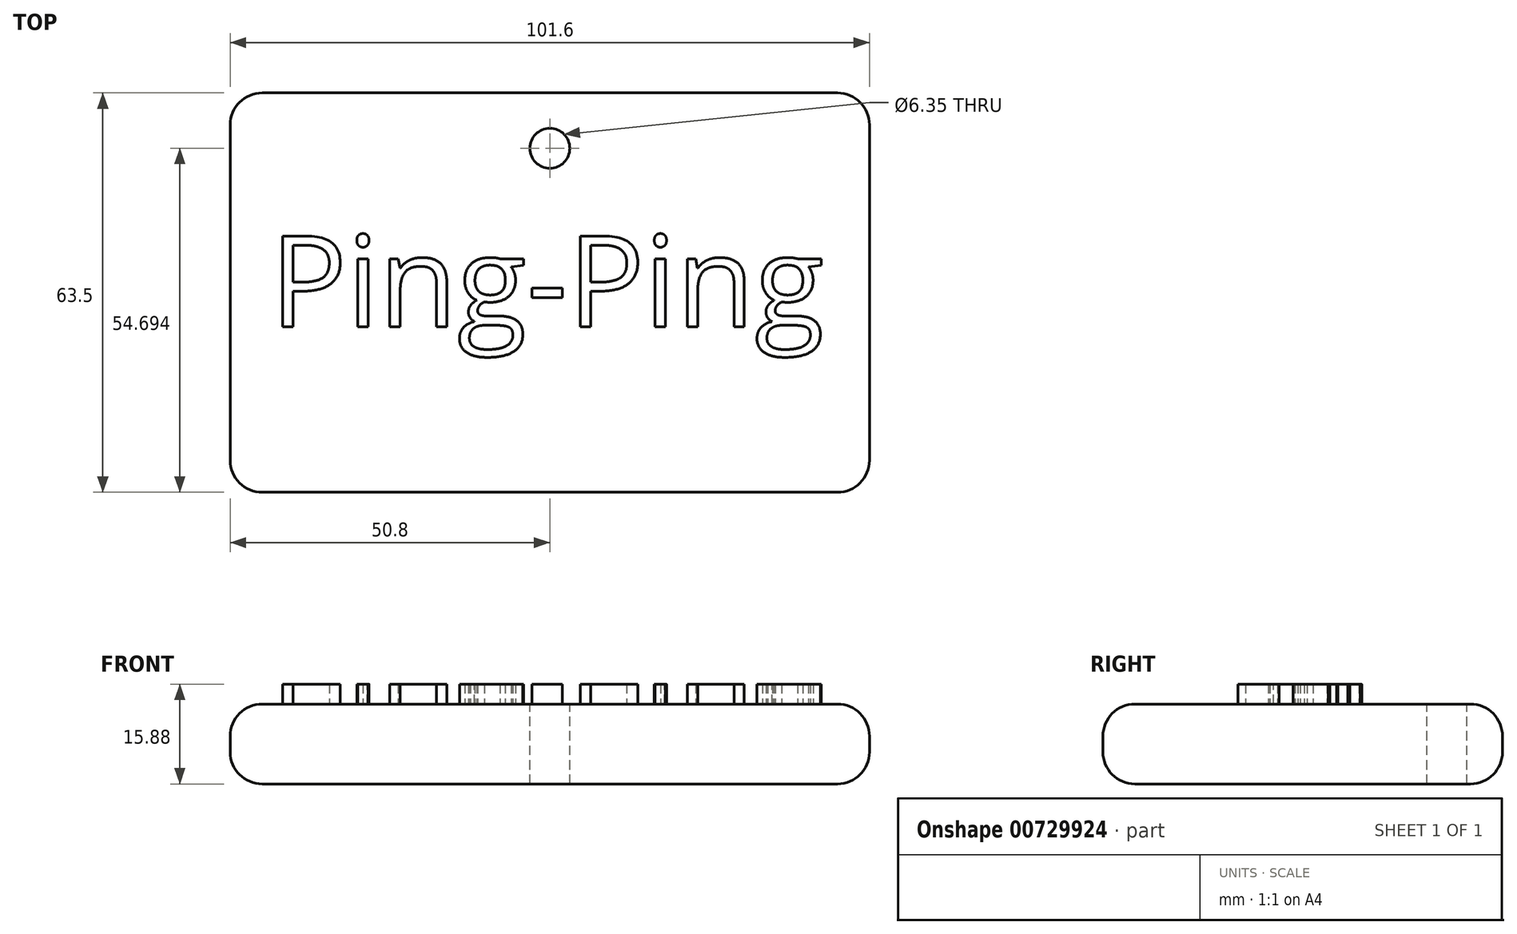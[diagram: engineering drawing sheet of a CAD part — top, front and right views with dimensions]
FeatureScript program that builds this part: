
annotation { "Feature Type Name" : "Feature", "Feature Type Description" : "" }
export const myFeature = defineFeature(function(context is Context, id is Id, definition is map)
    precondition{}
    {
        {
            var Q0;
            Q0=qCreatedBy(makeId("Top.planeOp"),FACE);
            var sketch = newSketch(context, id + "F0", { "sketchPlane" : qUnion([Q0])});
            skLineSegment(sketch, "E0.bottom", {"start": v(-50.8, -31.75) * mm, "end": v(50.8, -31.75) * mm});
            skLineSegment(sketch, "E0.top", {"start": v(-50.8, 31.75) * mm, "end": v(50.8, 31.75) * mm});
            skLineSegment(sketch, "E0.left", {"start": v(-50.8, -31.75) * mm, "end": v(-50.8, 31.75) * mm});
            skLineSegment(sketch, "E0.right", {"start": v(50.8, -31.75) * mm, "end": v(50.8, 31.75) * mm});
            skPoint(sketch, "E0.middle", {"position": v(0, 0) * mm});
            skSolve(sketch);
        }
        {
            var Q0;
            Q0=makeQuery(id+"F0.imprint","IMPRINT",FACE,{"disambiguationData":[TD([[makeQuery(id+"F0.imprint","IMPRINT",EDGE,{"derivedFrom":sQuery(id+"F0.wireOp",EDGE,"E0.bottom")}),1.0]])]});
            extrude(context, id + "F1", {"entities" : qUnion([Q0]), "depth" : 12.7 * mm, "offsetDistance" : 25.4 * mm});
        }
        {
            var Q0;
            Q0=makeQuery(id+"F1.opExtrude","CAP_FACE",FACE,{"disambiguationData":[OSD([sQuery(id+"F0.wireOp",EDGE,"E0.bottom"),sQuery(id+"F0.wireOp",EDGE,"E0.top"),sQuery(id+"F0.wireOp",EDGE,"E0.left"),sQuery(id+"F0.wireOp",EDGE,"E0.right")])],"isStart":false});
            var sketch = newSketch(context, id + "F2", { "sketchPlane" : qUnion([Q0])});
            skText(sketch, "E1", { "text": "Ping-Ping", "fontName": "OpenSans-Regular.ttf"});
            const initialGuessF2  = {"E1": [-0.04445, -0.00545, 1, 0, 0.01456]};
            skSetInitialGuess(sketch, initialGuessF2);
            skSolve(sketch);
        }
        {
            var Q0;
            Q0 = qSketchRegion(id + "F2", true);
            extrude(context, id + "F3", {"entities" : qUnion([Q0]), "operationType" : NewBodyOperationType.ADD, "depth" : 3.17 * mm, "offsetDistance" : 25.4 * mm});
        }
        {
            var Q0;
            {var subQ0=sQuery(id+"F0.wireOp",EDGE,"E0.top");var subQ1=sQuery(id+"F0.wireOp",EDGE,"E0.right");var subQ2=sQuery(id+"F0.wireOp",EDGE,"E0.bottom");var subQ3=sQuery(id+"F0.wireOp",EDGE,"E0.left");Q0=makeQuery(id+"F3.boolean.opBoolean","SPLIT",FACE,{"disambiguationData":[TD([makeQuery(id+"F1.opExtrude","SWEPT_FACE",FACE,{"disambiguationData":[OSD([subQ2])]})])],"derivedFrom":makeQuery(id+"F1.opExtrude","CAP_FACE",FACE,{"disambiguationData":[OSD([subQ2,subQ0,subQ3,subQ1])],"isStart":false})});}
            var sketch = newSketch(context, id + "F4", { "sketchPlane" : qUnion([Q0])});
            skCircle(sketch, "E2", {"center": v(0, 22.94) * mm, "radius": 3.18 * mm});
            skLineSegment(sketch, "E3", {"start": v(0, 22.94) * mm, "end": v(0, 31.75) * mm, "construction": true});
            skSolve(sketch);
        }
        {
            var Q0;
            Q0=makeQuery(id+"F4.imprint","IMPRINT",FACE,{"disambiguationData":[TD([[makeQuery(id+"F4.imprint","IMPRINT",EDGE,{"derivedFrom":sQuery(id+"F4.wireOp",EDGE,"E2")}),1.0]])]});
            extrude(context, id + "F5", {"entities" : qUnion([Q0]), "operationType" : NewBodyOperationType.REMOVE, "endBound" : BoundingType.THROUGH_ALL, "oppositeDirection" : true, "depth" : 25.4 * mm, "offsetDistance" : 25.4 * mm});
        }
        {
            var Q0;
            Q0=makeQuery(id+"F1.opExtrude","SWEPT_EDGE",EDGE,{"disambiguationData":[OSD([sQuery(id+"F0.wireOp",EDGE,"E0.top"),sQuery(id+"F0.wireOp",EDGE,"E0.right")])]});
            var Q1;
            Q1=makeQuery(id+"F1.opExtrude","SWEPT_EDGE",EDGE,{"disambiguationData":[OSD([sQuery(id+"F0.wireOp",EDGE,"E0.top"),sQuery(id+"F0.wireOp",EDGE,"E0.left")])]});
            var Q2;
            Q2=makeQuery(id+"F1.opExtrude","SWEPT_EDGE",EDGE,{"disambiguationData":[OSD([sQuery(id+"F0.wireOp",EDGE,"E0.bottom"),sQuery(id+"F0.wireOp",EDGE,"E0.right")])]});
            var Q3;
            Q3=makeQuery(id+"F1.opExtrude","SWEPT_EDGE",EDGE,{"disambiguationData":[OSD([sQuery(id+"F0.wireOp",EDGE,"E0.bottom"),sQuery(id+"F0.wireOp",EDGE,"E0.left")])]});
            fillet(context, id + "F6", {"entities" : qUnion([Q0, Q1, Q2, Q3]), "radius" : 5.08 * mm, "tangentPropagation" : true, "allowEdgeOverflow" : false});
        }
        {
            var Q0;
            Q0=makeQuery(id+"F1.opExtrude","CAP_EDGE",EDGE,{"disambiguationData":[OSD([sQuery(id+"F0.wireOp",EDGE,"E0.right")])],"isStart":false});
            var Q1;
            {var subQ0=sQuery(id+"F0.wireOp",EDGE,"E0.top");var subQ1=sQuery(id+"F0.wireOp",EDGE,"E0.right");var subQ2=sQuery(id+"F0.wireOp",EDGE,"E0.bottom");var subQ3=sQuery(id+"F0.wireOp",EDGE,"E0.left");Q1=makeQuery(id+"F6.opFillet","BLEND_EDGE",EDGE,{"blendedFrom":[makeQuery(id+"F1.opExtrude","SWEPT_EDGE",EDGE,{"disambiguationData":[OSD([subQ2,subQ1])]}),makeQuery(id+"F3.boolean.opBoolean","SPLIT",FACE,{"disambiguationData":[TD([makeQuery(id+"F1.opExtrude","SWEPT_FACE",FACE,{"disambiguationData":[OSD([subQ2])]})])],"derivedFrom":makeQuery(id+"F1.opExtrude","CAP_FACE",FACE,{"disambiguationData":[OSD([subQ2,subQ0,subQ3,subQ1])],"isStart":false})})],"blendedInto":[makeQuery(id+"F3.boolean.opBoolean","SPLIT",FACE,{"disambiguationData":[TD([makeQuery(id+"F1.opExtrude","SWEPT_FACE",FACE,{"disambiguationData":[OSD([subQ2])]})])],"derivedFrom":makeQuery(id+"F1.opExtrude","CAP_FACE",FACE,{"disambiguationData":[OSD([subQ2,subQ0,subQ3,subQ1])],"isStart":false})})]});}
            var Q2;
            Q2=makeQuery(id+"F1.opExtrude","CAP_EDGE",EDGE,{"disambiguationData":[OSD([sQuery(id+"F0.wireOp",EDGE,"E0.right")])],"isStart":true});
            var Q3;
            {var subQ0=sQuery(id+"F0.wireOp",EDGE,"E0.right");var subQ1=sQuery(id+"F0.wireOp",EDGE,"E0.top");Q3=makeQuery(id+"F6.opFillet","BLEND_EDGE",EDGE,{"blendedFrom":[makeQuery(id+"F1.opExtrude","SWEPT_EDGE",EDGE,{"disambiguationData":[OSD([subQ1,subQ0])]}),makeQuery(id+"F1.opExtrude","CAP_FACE",FACE,{"disambiguationData":[OSD([sQuery(id+"F0.wireOp",EDGE,"E0.bottom"),subQ1,sQuery(id+"F0.wireOp",EDGE,"E0.left"),subQ0])],"isStart":true})],"blendedInto":[makeQuery(id+"F1.opExtrude","CAP_FACE",FACE,{"disambiguationData":[OSD([sQuery(id+"F0.wireOp",EDGE,"E0.bottom"),subQ1,sQuery(id+"F0.wireOp",EDGE,"E0.left"),subQ0])],"isStart":true})]});}
            fillet(context, id + "F7", {"entities" : qUnion([Q0, Q1, Q2, Q3]), "radius" : 5.08 * mm, "tangentPropagation" : true, "allowEdgeOverflow" : false});
        }
    });
